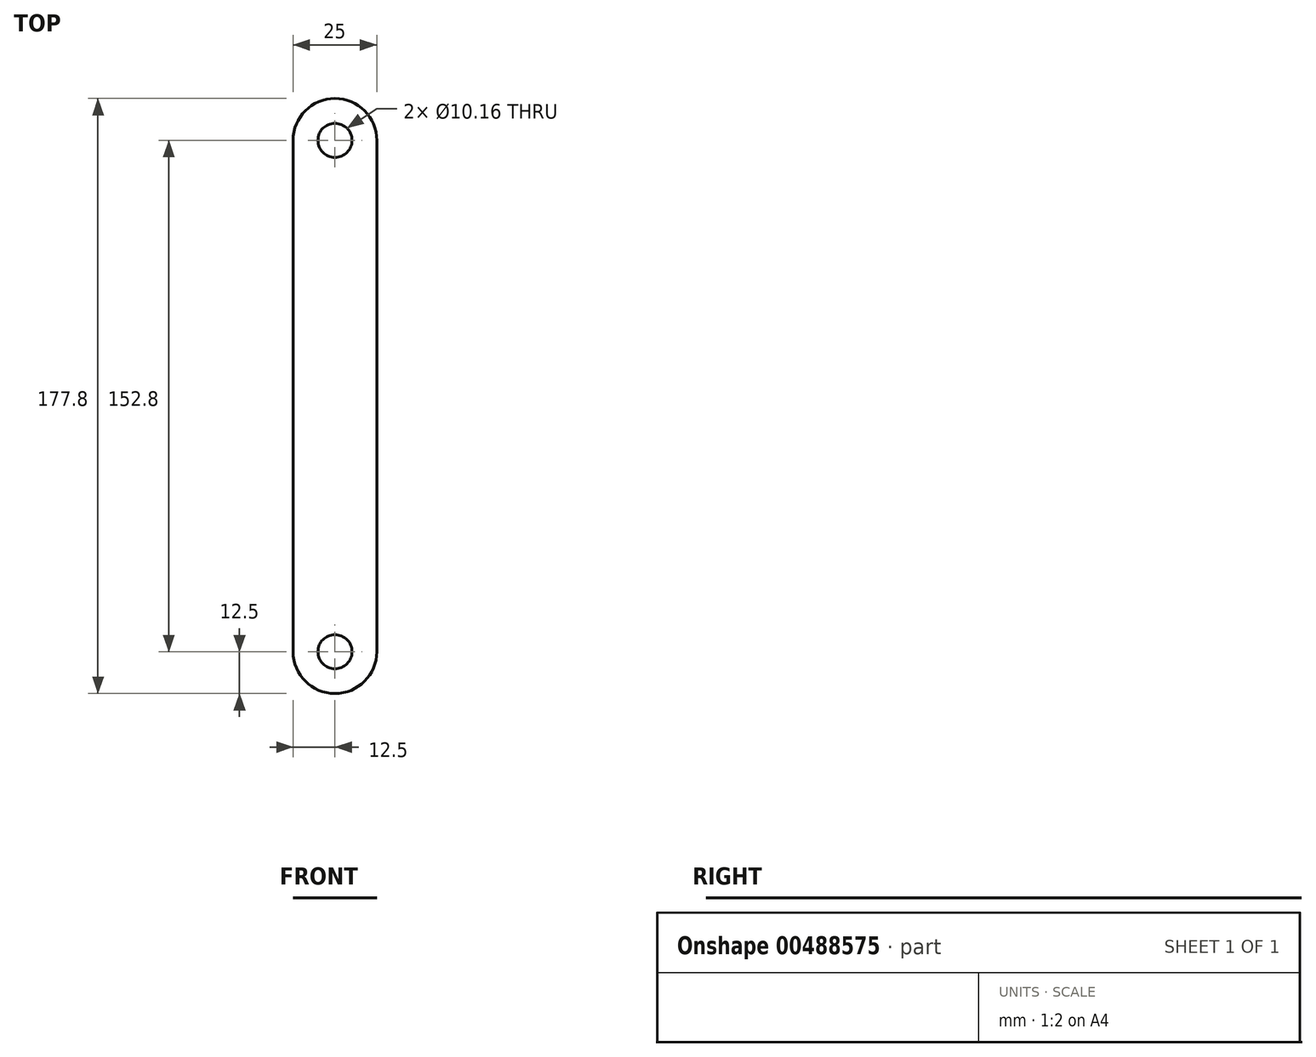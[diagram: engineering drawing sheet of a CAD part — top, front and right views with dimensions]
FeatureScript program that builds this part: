
annotation { "Feature Type Name" : "Feature", "Feature Type Description" : "" }
export const myFeature = defineFeature(function(context is Context, id is Id, definition is map)
    precondition{}
    {
        {
            var Q0;
            Q0=qCreatedBy(makeId("Top.planeOp"),FACE);
            var sketch = newSketch(context, id + "F0", { "sketchPlane" : qUnion([Q0])});
            skLineSegment(sketch, "E0.bottom", {"start": v(0, 88.9) * mm, "end": v(0, 88.9) * mm});
            skLineSegment(sketch, "E0.top", {"start": v(0, -88.9) * mm, "end": v(0, -88.9) * mm});
            skLineSegment(sketch, "E0.left", {"start": v(12.5, 76.4) * mm, "end": v(12.5, -76.4) * mm});
            skLineSegment(sketch, "E0.right", {"start": v(-12.5, 76.4) * mm, "end": v(-12.5, -76.4) * mm});
            skPoint(sketch, "E0.middle", {"position": v(0, 0) * mm});
            skPoint(sketch, "E1.visualSharp", {"position": v(12.5, 88.9) * mm});
            skArc(sketch, "E1.filletArc", {"start": v(12.5, 76.4) * mm, "mid": v(8.84, 85.24) * mm, "end": v(0, 88.9) * mm});
            skPoint(sketch, "E2.visualSharp", {"position": v(-12.5, 88.9) * mm});
            skArc(sketch, "E2.filletArc", {"start": v(0, 88.9) * mm, "mid": v(-8.84, 85.24) * mm, "end": v(-12.5, 76.4) * mm});
            skPoint(sketch, "E3.visualSharp", {"position": v(-12.5, -88.9) * mm});
            skArc(sketch, "E3.filletArc", {"start": v(-12.5, -76.4) * mm, "mid": v(-8.84, -85.24) * mm, "end": v(0, -88.9) * mm});
            skPoint(sketch, "E4.visualSharp", {"position": v(12.5, -88.9) * mm});
            skArc(sketch, "E4.filletArc", {"start": v(0, -88.9) * mm, "mid": v(8.84, -85.24) * mm, "end": v(12.5, -76.4) * mm});
            skCircle(sketch, "E5", {"center": v(0, 76.4) * mm, "radius": 5.08 * mm});
            skLineSegment(sketch, "E6", {"start": v(-12.5, 0) * mm, "end": v(12.5, 0) * mm, "construction": true});
            skCircle(sketch, "E7.MirrorC", {"center": v(0, -76.4) * mm, "radius": 5.08 * mm});
            skSolve(sketch);
        }
        {
            var Q0;
            Q0=makeQuery(id+"F0.imprint","IMPRINT",FACE,{"disambiguationData":[TD([[makeQuery(id+"F0.imprint","IMPRINT",EDGE,{"derivedFrom":sQuery(id+"F0.wireOp",EDGE,"E0.left")}),-1.0]])]});
            extrude(context, id + "F1", {"entities" : qUnion([Q0]), "depth" : 1 / 203.2 * mm});
        }
    });
